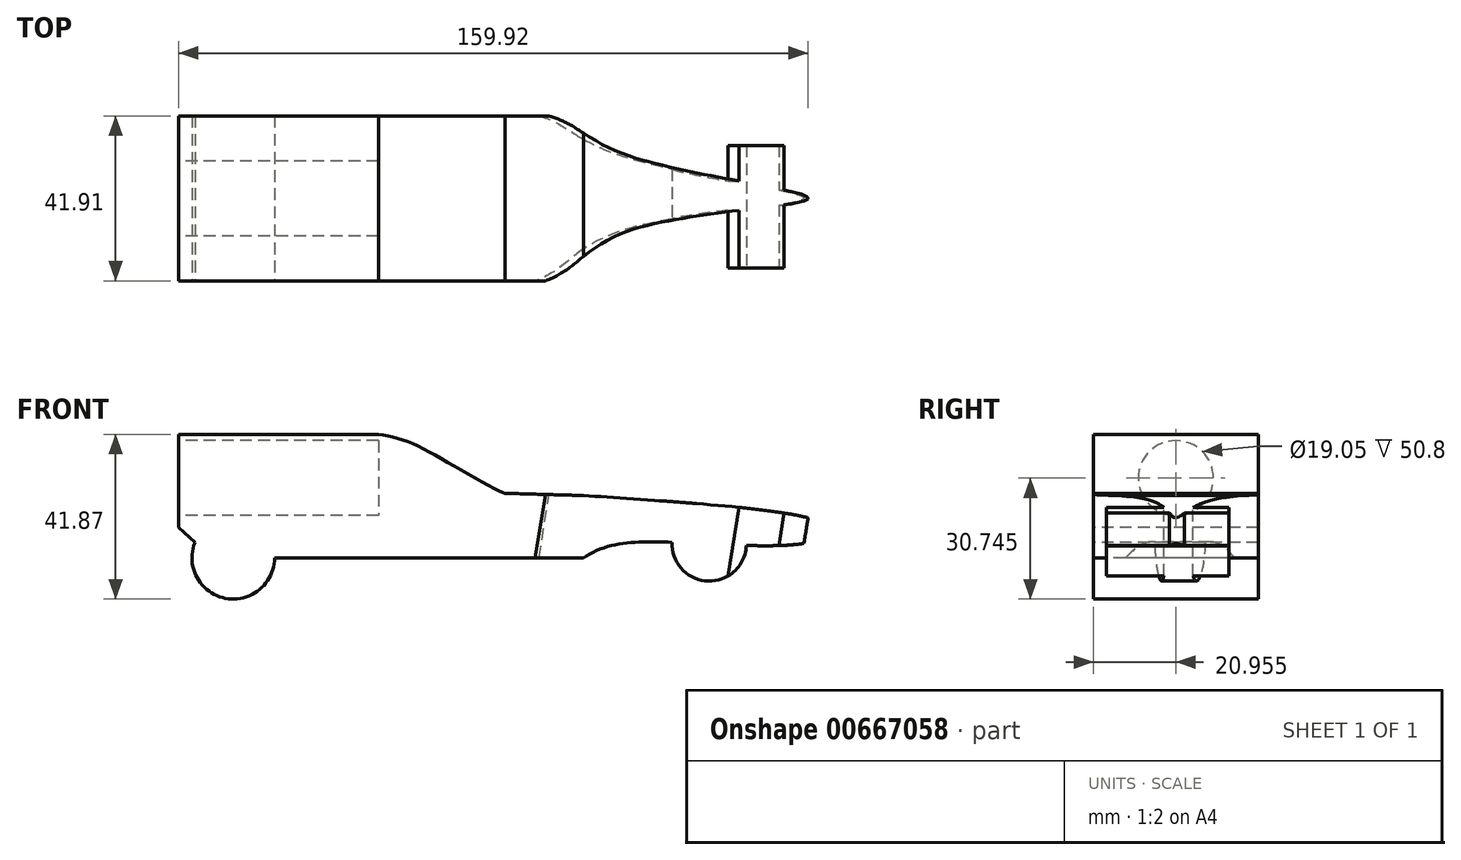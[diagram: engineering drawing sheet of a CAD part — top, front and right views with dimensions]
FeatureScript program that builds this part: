
annotation { "Feature Type Name" : "Feature", "Feature Type Description" : "" }
export const myFeature = defineFeature(function(context is Context, id is Id, definition is map)
    precondition{}
    {
        {
            var Q0;
            Q0=qCreatedBy(makeId("Front.planeOp"),FACE);
            var sketch = newSketch(context, id + "F0", { "sketchPlane" : qUnion([Q0])});
            skLineSegment(sketch, "E0", {"start": v(0, 0) * mm, "end": v(304.8, 0) * mm});
            skLineSegment(sketch, "E1", {"start": v(304.8, 0) * mm, "end": v(304.8, 20.32) * mm});
            skLineSegment(sketch, "E2", {"start": v(304.8, 20.32) * mm, "end": v(0, 69.34) * mm});
            skLineSegment(sketch, "E3", {"start": v(0, 69.34) * mm, "end": v(0, 0) * mm});
            skSolve(sketch);
        }
        {
            var Q0;
            Q0=makeQuery(id+"F0.imprint","IMPRINT",FACE,{"disambiguationData":[TD([[makeQuery(id+"F0.imprint","IMPRINT",EDGE,{"derivedFrom":sQuery(id+"F0.wireOp",EDGE,"E0")}),1.0]])]});
            extrude(context, id + "F1", {"entities" : qUnion([Q0]), "depth" : 41.9 * mm, "offsetDistance" : 25.4 * mm});
        }
        {
            var Q0;
            Q0=makeQuery(id+"F1.opExtrude","SWEPT_FACE",FACE,{"disambiguationData":[OSD([sQuery(id+"F0.wireOp",EDGE,"E3")])]});
            var sketch = newSketch(context, id + "F2", { "sketchPlane" : qUnion([Q0])});
            skCircle(sketch, "E4", {"center": v(20.96, 33.66) * mm, "radius": 9.53 * mm});
            skSolve(sketch);
        }
        {
            var Q0;
            Q0=makeQuery(id+"F2.imprint","IMPRINT",FACE,{"disambiguationData":[TD([[makeQuery(id+"F2.imprint","IMPRINT",EDGE,{"derivedFrom":sQuery(id+"F2.wireOp",EDGE,"E4")}),1.0]])]});
            extrude(context, id + "F3", {"entities" : qUnion([Q0]), "operationType" : NewBodyOperationType.REMOVE, "oppositeDirection" : true, "depth" : 50.8 * mm, "offsetDistance" : 25.4 * mm});
        }
        {
            var Q0;
            Q0=makeQuery(id+"F1.opExtrude","CAP_FACE",FACE,{"disambiguationData":[OSD([sQuery(id+"F0.wireOp",EDGE,"E0"),sQuery(id+"F0.wireOp",EDGE,"E1"),sQuery(id+"F0.wireOp",EDGE,"E2"),sQuery(id+"F0.wireOp",EDGE,"E3")])],"isStart":false});
            var sketch = newSketch(context, id + "F4", { "sketchPlane" : qUnion([Q0])});
            skPoint(sketch, "E5.3.internal.snap0", {"position": v(0, 34.67) * mm});
            skFitSpline(sketch, "E6", {"points": [v(0, 21.05) * mm, v(5.8, 26.56) * mm, v(102.82, 29.21) * mm], "startDerivative": vector(15, 27.05) * mm, "endDerivative": vector(163.27, -4.84) * mm});
            skLineSegment(sketch, "E7", {"start": v(0, 44.78) * mm, "end": v(50.78, 44.78) * mm});
            skFitSpline(sketch, "E8", {"points": [v(50.78, 44.78) * mm, v(58.71, 42.72) * mm, v(71.9, 35.61) * mm, v(82.9, 29.78) * mm, v(83.12, 29.78) * mm], "startDerivative": vector(28.78, -5.35) * mm, "endDerivative": vector(3.19, 0.95) * mm});
            skLineSegment(sketch, "E9", {"start": v(0, 21.05) * mm, "end": v(8.5, 13.4) * mm});
            skLineSegment(sketch, "E10", {"start": v(8.5, 13.4) * mm, "end": v(102.82, 13.4) * mm});
            skLineSegment(sketch, "E11", {"start": v(0, 44.78) * mm, "end": v(0, 21.05) * mm});
            skPoint(sketch, "E12.1.internal.snap0", {"position": v(4.25, 17.23) * mm});
            skPoint(sketch, "E12.2.internal.snap0", {"position": v(4.25, 17.23) * mm});
            skFitSpline(sketch, "E12", {"points": [v(102.82, 13.4) * mm, v(114.45, 17.23) * mm, v(159.82, 17.23) * mm, v(165.35, 21.05) * mm, v(102.82, 29.21) * mm], "startDerivative": vector(50.24, 29.38) * mm, "endDerivative": vector(-236.17, 15.46) * mm});
            skArc(sketch, "E13", {"start": v(130.61, 17.12) * mm, "mid": v(134.8, 13.3) * mm, "end": v(139.32, 16.72) * mm});
            skLineSegment(sketch, "E14", {"start": v(146.53, 19.04) * mm, "end": v(158.78, 19.04) * mm});
            skLineSegment(sketch, "E15", {"start": v(158.78, 19.04) * mm, "end": v(158.78, 17.23) * mm});
            skLineSegment(sketch, "E16", {"start": v(158.78, 17.23) * mm, "end": v(146.53, 17.23) * mm});
            skLineSegment(sketch, "E17", {"start": v(146.53, 17.23) * mm, "end": v(146.53, 19.04) * mm});
            skCircle(sketch, "E18", {"center": v(13.87, 13.4) * mm, "radius": 10.5 * mm});
            skCircle(sketch, "E19", {"center": v(134.8, 16.92) * mm, "radius": 9.45 * mm});
            skPoint(sketch, "E19.centerSnap0", {"position": v(134.8, 13.3) * mm});
            skSolve(sketch);
        }
        {
            var Q0;
            Q0=makeQuery(id+"F1.opExtrude","SWEPT_FACE",FACE,{"disambiguationData":[OSD([sQuery(id+"F0.wireOp",EDGE,"E2")])]});
            var sketch = newSketch(context, id + "F5", { "sketchPlane" : qUnion([Q0])});
            skPoint(sketch, "E20.6.internal.snap0", {"position": v(-11.01, -20.96) * mm});
            skFitSpline(sketch, "E20", {"points": [v(-11.01, -20.96) * mm, v(-6.1, -14.53) * mm, v(10.68, -6.09) * mm, v(39.5, 0) * mm, v(88.28, 0) * mm, v(107.91, -10) * mm, v(154.15, -20.95) * mm, v(107.91, -29.38) * mm, v(87.33, -41.91) * mm, v(39.82, -41.91) * mm, v(9.89, -41.91) * mm, v(-6.74, -35.17) * mm, v(-11.01, -20.96) * mm]});
            skLineSegment(sketch, "E21.bottom", {"start": v(136.42, -7.5) * mm, "end": v(147.98, -7.5) * mm});
            skLineSegment(sketch, "E21.top", {"start": v(136.42, -38.6) * mm, "end": v(147.98, -38.6) * mm});
            skLineSegment(sketch, "E21.left", {"start": v(136.42, -7.5) * mm, "end": v(136.42, -38.6) * mm});
            skLineSegment(sketch, "E21.right", {"start": v(147.98, -7.5) * mm, "end": v(147.98, -38.6) * mm});
            skFitSpline(sketch, "E22", {"points": [v(-9.73, -17.82) * mm, v(43.3, -14.53) * mm, v(48.69, -26.25) * mm, v(-11.01, -28.6) * mm, v(-10.48, -27.92) * mm], "startDerivative": vector(164.62, 37.04) * mm, "endDerivative": vector(23.97, 14) * mm});
            skSolve(sketch);
        }
        {
            var Q0;
            {var subQ4=sQuery(id+"F5.wireOp",EDGE,"E21.bottom");Q0=makeQuery(id+"F5.imprint","IMPRINT",FACE,{"disambiguationData":[TD([[makeQuery(id+"F5.imprint","IMPRINT",EDGE,{"derivedFrom":subQ4}),1.0]])]});}
            extrude(context, id + "F6", {"entities" : qUnion([Q0]), "operationType" : NewBodyOperationType.REMOVE, "oppositeDirection" : true, "depth" : 50.8 * mm, "offsetDistance" : 25.4 * mm});
        }
        {
            var Q0;
            Q0=makeQuery(id+"F1.opExtrude","SWEPT_FACE",FACE,{"disambiguationData":[OSD([sQuery(id+"F0.wireOp",EDGE,"E1")])]});
            extrude(context, id + "F7", {"entities" : qUnion([Q0]), "operationType" : NewBodyOperationType.REMOVE, "oppositeDirection" : true, "depth" : 25.4 * mm, "offsetDistance" : 25.4 * mm});
        }
        {
            var Q0;
            {var subQ14=sQuery(id+"F4.wireOp",EDGE,"E7");Q0=makeQuery(id+"F4.imprint","IMPRINT",FACE,{"disambiguationData":[TD([[makeQuery(id+"F4.imprint","IMPRINT",EDGE,{"derivedFrom":subQ14}),1.0]])]});}
            extrude(context, id + "F8", {"entities" : qUnion([Q0]), "operationType" : NewBodyOperationType.REMOVE, "oppositeDirection" : true, "depth" : 50.8 * mm, "offsetDistance" : 25.4 * mm});
        }
    });
